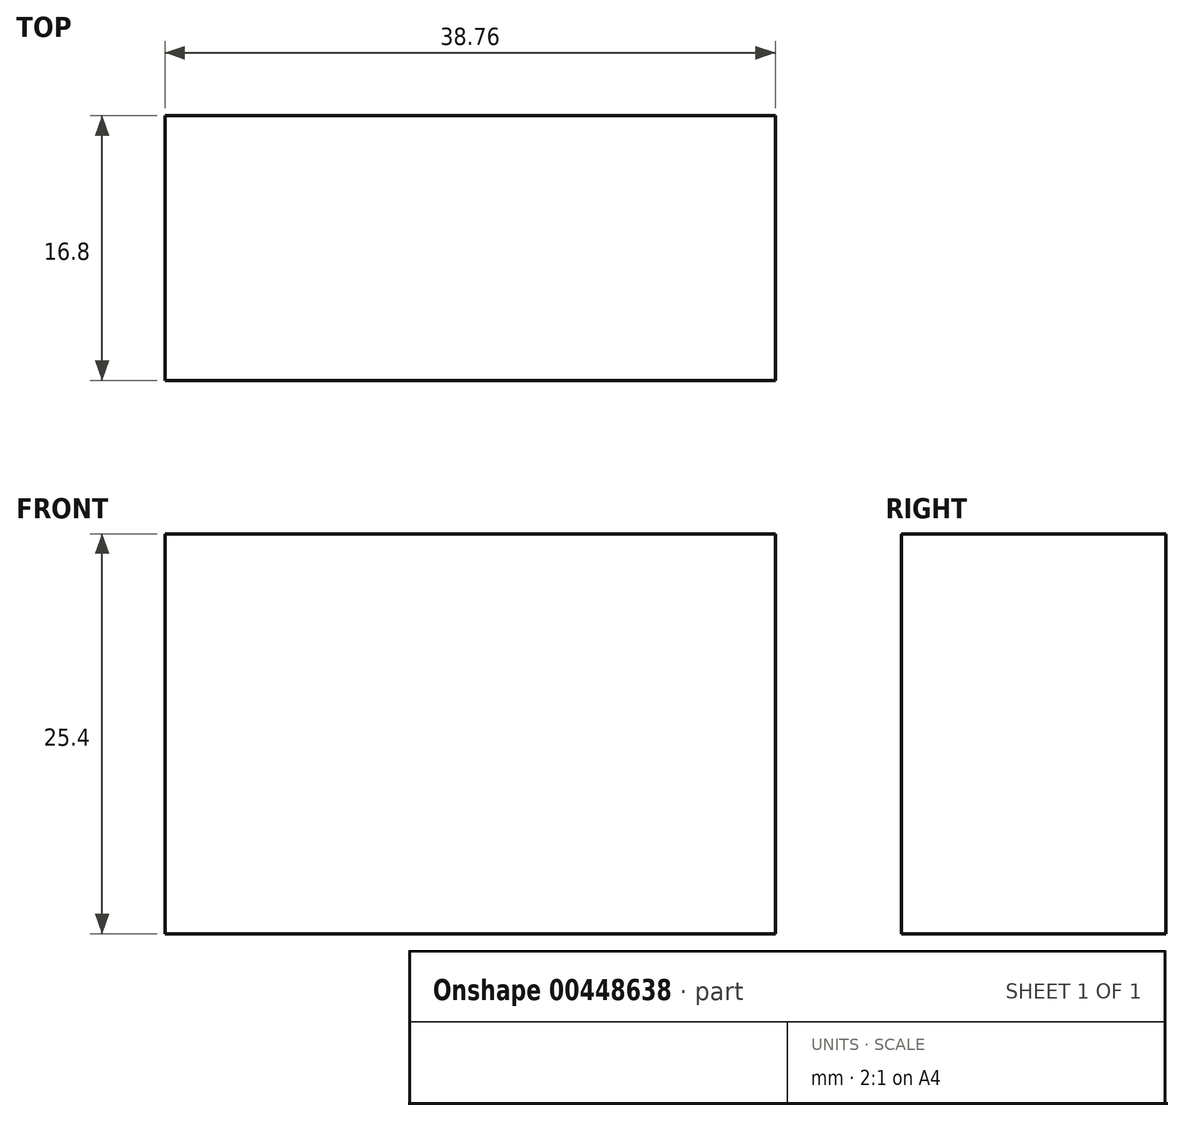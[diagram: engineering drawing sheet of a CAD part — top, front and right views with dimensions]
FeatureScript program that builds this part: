
annotation { "Feature Type Name" : "Feature", "Feature Type Description" : "" }
export const myFeature = defineFeature(function(context is Context, id is Id, definition is map)
    precondition{}
    {
        {
            var Q0;
            Q0=qCreatedBy(makeId("Top.planeOp"),FACE);
            var sketch = newSketch(context, id + "F0", { "sketchPlane" : qUnion([Q0])});
            skLineSegment(sketch, "E0.bottom", {"start": v(-67.46, -51.55) * mm, "end": v(-28.7, -51.55) * mm});
            skLineSegment(sketch, "E0.top", {"start": v(-67.46, -68.35) * mm, "end": v(-28.7, -68.35) * mm});
            skLineSegment(sketch, "E0.left", {"start": v(-67.46, -51.55) * mm, "end": v(-67.46, -68.35) * mm});
            skLineSegment(sketch, "E0.right", {"start": v(-28.7, -51.55) * mm, "end": v(-28.7, -68.35) * mm});
            skSolve(sketch);
        }
        {
            var Q0;
            Q0=makeQuery(id+"F0.imprint","IMPRINT",FACE,{"disambiguationData":[TD([[makeQuery(id+"F0.imprint","IMPRINT",EDGE,{"derivedFrom":sQuery(id+"F0.wireOp",EDGE,"E0.bottom")}),-1.0]])]});
            extrude(context, id + "F1", {"entities" : qUnion([Q0]), "depth" : 25.4 * mm});
        }
    });
